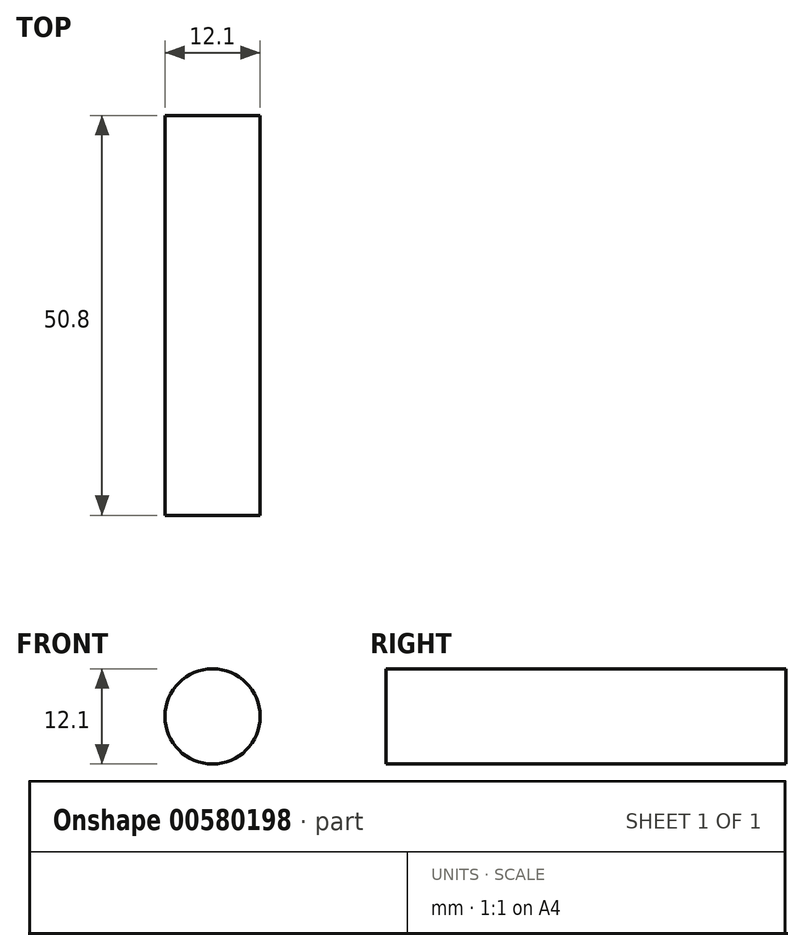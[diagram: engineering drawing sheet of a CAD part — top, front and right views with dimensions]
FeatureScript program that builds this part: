
annotation { "Feature Type Name" : "Feature", "Feature Type Description" : "" }
export const myFeature = defineFeature(function(context is Context, id is Id, definition is map)
    precondition{}
    {
        {
            var Q0;
            Q0=qCreatedBy(makeId("Front.planeOp"),FACE);
            var sketch = newSketch(context, id + "F0", { "sketchPlane" : qUnion([Q0])});
            skCircle(sketch, "E0", {"center": v(0, 0) * mm, "radius": 6.05 * mm});
            skSolve(sketch);
        }
        {
            var Q0;
            Q0=makeQuery(id+"F0.imprint","IMPRINT",FACE,{"disambiguationData":[TD([[makeQuery(id+"F0.imprint","IMPRINT",EDGE,{"derivedFrom":sQuery(id+"F0.wireOp",EDGE,"E0")}),1.0]])]});
            extrude(context, id + "F1", {"entities" : qUnion([Q0]), "depth" : 50.8 * mm, "offsetDistance" : 25.4 * mm});
        }
    });
